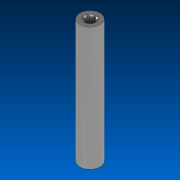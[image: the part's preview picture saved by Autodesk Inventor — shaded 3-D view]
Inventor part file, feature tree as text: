
AUTODESK INVENTOR PART (.ipt)
format: ipt  version: 2022.2 (Build 262287000, 287)  size: 664,064 bytes
history: native  units: in
note: dims shown in document units (in); Inventor stores cm internally (conversion verified against a paired STEP export)
features: extrude x2, sketch x2, other x1, projected_geometry x1
ambient origin geometry x8: Origin, YZ Plane, XZ Plane, XY Plane, X Axis, Y Axis, Z Axis, Center Point
bodies: Solid1 (feature_tree)
feature tree (6):
  extrude  "Extrusion1"  Depth=1.0in TaperAngle=0.0deg
  extrude  "Extrusion2"  [1 undecoded]
  sketch  "Sketch1"  dims[d0=0.164in d1=1.0in d2=0.0in]
  sketch  "Sketch2"  dims[d3=1.0in d4=0.0in]
  other  "Cut-Revolve7"
  projected_geometry  "Project Cut Edges1"
note: 1 required parameter value undecoded (feature->parameter linkage not recoverable at this tier; creation-order binding heuristic only, values carry confidence <= 0.55)
